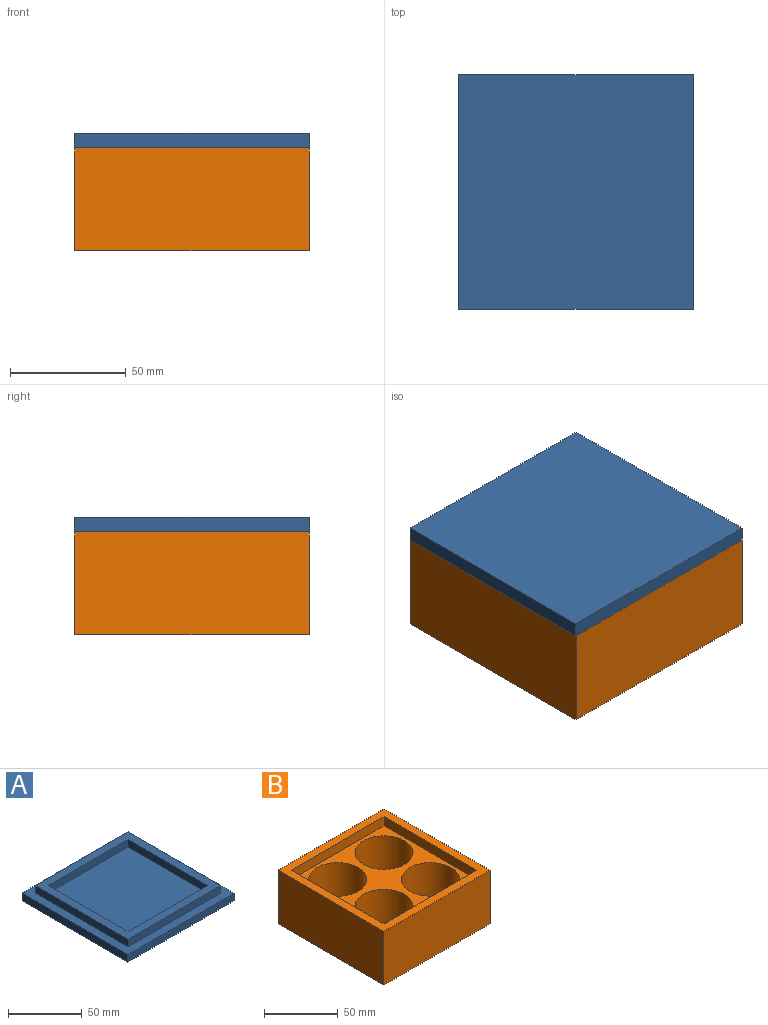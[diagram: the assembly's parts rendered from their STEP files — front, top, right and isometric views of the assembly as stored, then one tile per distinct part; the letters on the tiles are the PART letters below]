
ASSEMBLY  parts=2 mates=1
PART A: 16 faces, bbox 101.6x101.6x12.7 mm
  f0: plane 101.6x101.6mm, normal (0,0,1), area 2419.3mm2, adj f1,f2,f3,f4,f9,f10,f11,f12
  f1: plane 101.6x6.35mm, normal (1,0,0), area 645.2mm2, adj f0,f2,f4,f5
  f2: plane 101.6x6.35mm, normal (0,1,0), area 645.2mm2, adj f0,f1,f3,f5
  f3: plane 101.6x6.35mm, normal (-1,0,0), area 645.2mm2, adj f0,f2,f4,f5
  f4: plane 101.6x6.35mm, normal (0,-1,0), area 645.2mm2, adj f0,f1,f3,f5
  f5: plane 101.6x101.6mm, normal (0,0,-1), area 10322.6mm2, adj f1,f2,f3,f4
  f6: plane 76.2x6.35mm, normal (-1,0,0), area 483.9mm2, adj f7,f13,f14,f15
  f7: plane 76.2x6.35mm, normal (0,1,0), area 483.9mm2, adj f6,f8,f14,f15
  f8: plane 76.2x6.35mm, normal (1,0,0), area 483.9mm2, adj f7,f13,f14,f15
  f9: plane 88.9x6.35mm, normal (0,-1,0), area 564.5mm2, adj f0,f10,f12,f14
  f10: plane 88.9x6.35mm, normal (1,0,0), area 564.5mm2, adj f0,f9,f11,f14
  f11: plane 88.9x6.35mm, normal (0,1,0), area 564.5mm2, adj f0,f10,f12,f14
  f12: plane 88.9x6.35mm, normal (-1,0,0), area 564.5mm2, adj f0,f9,f11,f14
  f13: plane 76.2x6.35mm, normal (0,-1,0), area 483.9mm2, adj f6,f8,f14,f15
  f14: plane 88.9x88.9mm, normal (0,0,1), area 2096.8mm2, adj f6,f7,f8,f9,f10,f11,f12,f13
  f15: plane 76.2x76.2mm, normal (0,0,1), area 5806.4mm2, adj f6,f7,f8,f13
PART B: 19 faces, bbox 101.6x101.6x44.5 mm
  f0: plane 101.6x44.45mm, normal (1,0,0), area 4516.1mm2, adj f1,f3,f4,f9
  f1: plane 101.6x44.45mm, normal (0,1,0), area 4516.1mm2, adj f0,f2,f4,f9
  f2: plane 101.6x44.45mm, normal (-1,0,0), area 4516.1mm2, adj f1,f3,f4,f9
  f3: plane 101.6x44.45mm, normal (0,-1,0), area 4516.1mm2, adj f0,f2,f4,f9
  f4: plane 101.6x101.6mm, normal (0,0,-1), area 10322.6mm2, adj f0,f1,f2,f3
  f5: plane 88.9x7.62mm, normal (1,0,0), area 677.4mm2, adj f6,f8,f9,f14
  f6: plane 88.9x7.62mm, normal (0,-1,0), area 677.4mm2, adj f5,f7,f9,f14
  f7: plane 88.9x7.62mm, normal (-1,0,0), area 677.4mm2, adj f6,f8,f9,f14
  f8: plane 88.9x7.62mm, normal (0,1,0), area 677.4mm2, adj f5,f7,f9,f14
  f9: plane 101.6x101.6mm, normal (0,0,1), area 2419.3mm2, adj f0,f1,f2,f3,f5,f6,f7,f8
  f10: cylinder r=19.69mm len=39.37mm, axis (0,0,-1), area 3769.9mm2, adj f14,f15
  f11: cylinder r=19.69mm len=39.37mm, axis (0,0,-1), area 3769.9mm2, adj f14,f16
  f12: cylinder r=19.69mm len=39.37mm, axis (0,0,-1), area 3769.9mm2, adj f14,f17
  f13: cylinder r=19.69mm len=39.37mm, axis (0,0,-1), area 3769.9mm2, adj f14,f18
  f14: plane 88.9x88.9mm, normal (0,0,1), area 3033.8mm2, adj f5,f6,f7,f8,f10,f11,f12,f13
  f15: plane 39.37x39.37mm, normal (0,0,1), area 1217.4mm2, adj f10
  f16: plane 39.37x39.37mm, normal (0,0,1), area 1217.4mm2, adj f11
  f17: plane 39.37x39.37mm, normal (0,0,1), area 1217.4mm2, adj f12
  f18: plane 39.37x39.37mm, normal (0,0,1), area 1217.4mm2, adj f13
PLACE A rot(axis=(0.71,0.71,0),180deg) t=(-18.45,0.06,43.65)mm
PLACE B t=(-18.45,0.06,-7.15)mm
MATE fastened A.f0 <-> B.f9  axis (0,0,-1) through (-69.25,-50.74,37.3)mm
